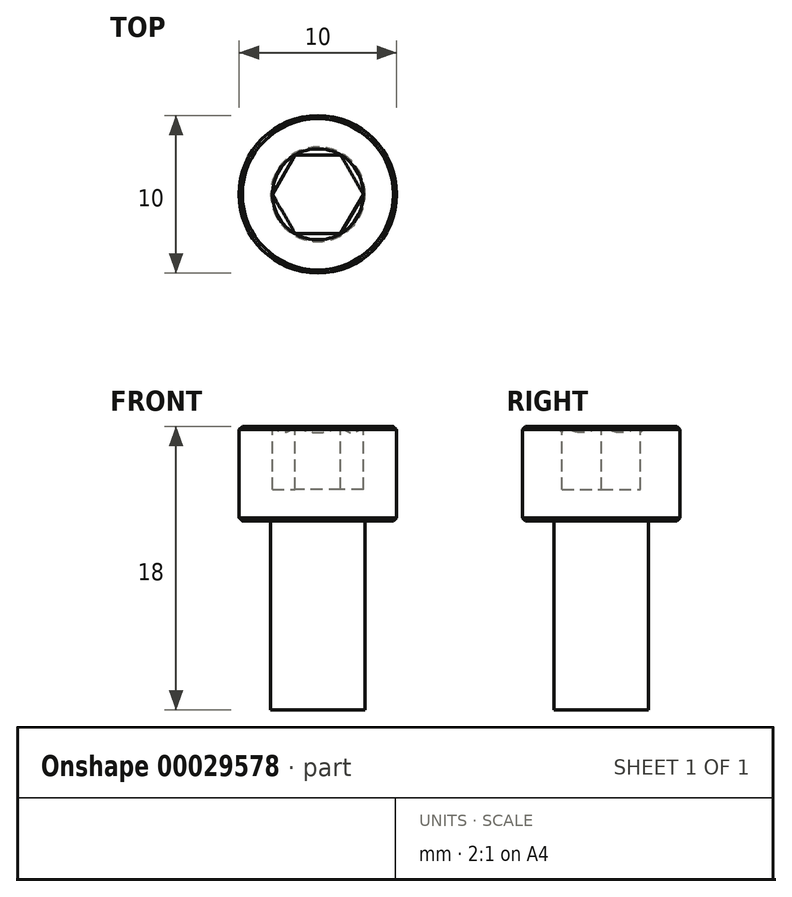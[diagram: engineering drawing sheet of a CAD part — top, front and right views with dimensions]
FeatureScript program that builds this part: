
annotation { "Feature Type Name" : "Feature", "Feature Type Description" : "" }
export const myFeature = defineFeature(function(context is Context, id is Id, definition is map)
    precondition{}
    {
        {
            var Q0;
            Q0=qCreatedBy(makeId("Front.planeOp"),FACE);
            var sketch = newSketch(context, id + "F0", { "sketchPlane" : qUnion([Q0])});
            skLineSegment(sketch, "E0", {"start": v(0, 17.39) * mm, "end": v(0, -18.17) * mm, "construction": true});
            skLineSegment(sketch, "E1", {"start": v(0, 6) * mm, "end": v(5, 6) * mm});
            skLineSegment(sketch, "E2", {"start": v(5, 6) * mm, "end": v(5, 0) * mm});
            skLineSegment(sketch, "E3", {"start": v(5, 0) * mm, "end": v(3, 0) * mm});
            skLineSegment(sketch, "E4", {"start": v(3, 0) * mm, "end": v(3, -12) * mm});
            skLineSegment(sketch, "E5", {"start": v(3, -12) * mm, "end": v(0, -12) * mm});
            skLineSegment(sketch, "E6", {"start": v(0, -12) * mm, "end": v(0, 6) * mm});
            skSolve(sketch);
        }
        {
            var Q0;
            Q0 = qSketchRegion(id + "F0", true);
            var Q1;
            Q1=sQuery(id+"F0.wireOp",EDGE,"E0");
            revolve(context, id + "F1", {"entities" : qUnion([Q0]), "axis" : qUnion([Q1]), "revolveType" : RevolveType.FULL});
        }
        {
            var Q0;
            Q0=makeQuery(id+"F1.opRevolve","SWEPT_FACE",FACE,{"disambiguationData":[OSD([sQuery(id+"F0.wireOp",EDGE,"E1")])]});
            var sketch = newSketch(context, id + "F2", { "sketchPlane" : qUnion([Q0])});
            skCircle(sketch, "E7.cCircle", {"center": v(0, 0) * mm, "radius": 2.5 * mm, "construction": true});
            skLineSegment(sketch, "E7.0", {"start": v(-2.89, 0) * mm, "end": v(-1.44, 2.5) * mm});
            skLineSegment(sketch, "E7.1", {"start": v(-1.44, 2.5) * mm, "end": v(1.44, 2.5) * mm});
            skLineSegment(sketch, "E7.2", {"start": v(1.44, 2.5) * mm, "end": v(2.89, 0) * mm});
            skLineSegment(sketch, "E7.3", {"start": v(2.89, 0) * mm, "end": v(1.44, -2.5) * mm});
            skLineSegment(sketch, "E7.4", {"start": v(1.44, -2.5) * mm, "end": v(-1.44, -2.5) * mm});
            skLineSegment(sketch, "E7.5", {"start": v(-1.44, -2.5) * mm, "end": v(-2.89, 0) * mm});
            skPoint(sketch, "E7.0.midPoint", {"position": v(-2.17, 1.25) * mm});
            skSolve(sketch);
        }
        {
            var Q0;
            Q0 = qSketchRegion(id + "F2", true);
            extrude(context, id + "F3", {"entities" : qUnion([Q0]), "operationType" : NewBodyOperationType.REMOVE, "oppositeDirection" : true, "depth" : 4 * mm});
        }
        {
            var Q0;
            Q0=qCreatedBy(makeId("Front.planeOp"),FACE);
            var sketch = newSketch(context, id + "F4", { "sketchPlane" : qUnion([Q0])});
            skLineSegment(sketch, "E8", {"start": v(2.5, 5.61) * mm, "end": v(2.89, 6) * mm});
            skLineSegment(sketch, "E9", {"start": v(2.5, 5.61) * mm, "end": v(2.5, 6) * mm});
            skLineSegment(sketch, "E10", {"start": v(2.5, 6) * mm, "end": v(2.89, 6) * mm});
            skLineSegment(sketch, "E11", {"start": v(0, 8.76) * mm, "end": v(0, 3.18) * mm, "construction": true});
            skSolve(sketch);
        }
        {
            var Q0;
            Q0 = qSketchRegion(id + "F4", true);
            var Q1;
            Q1=sQuery(id+"F4.wireOp",EDGE,"E11");
            revolve(context, id + "F5", {"operationType" : NewBodyOperationType.REMOVE, "entities" : qUnion([Q0]), "axis" : qUnion([Q1]), "revolveType" : RevolveType.FULL, "oppositeDirection" : true});
        }
        {
            var Q0;
            Q0=makeQuery(id+"F1.opRevolve","SWEPT_EDGE",EDGE,{"disambiguationData":[OSD([sQuery(id+"F0.wireOp",EDGE,"E1"),sQuery(id+"F0.wireOp",EDGE,"E2")])]});
            var Q1;
            Q1=makeQuery(id+"F1.opRevolve","SWEPT_EDGE",EDGE,{"disambiguationData":[OSD([sQuery(id+"F0.wireOp",EDGE,"E2"),sQuery(id+"F0.wireOp",EDGE,"E3")])]});
            chamfer(context, id + "F6", {"entities" : qUnion([Q0, Q1]), "width" : .2 * mm, "tangentPropagation" : true});
        }
    });
